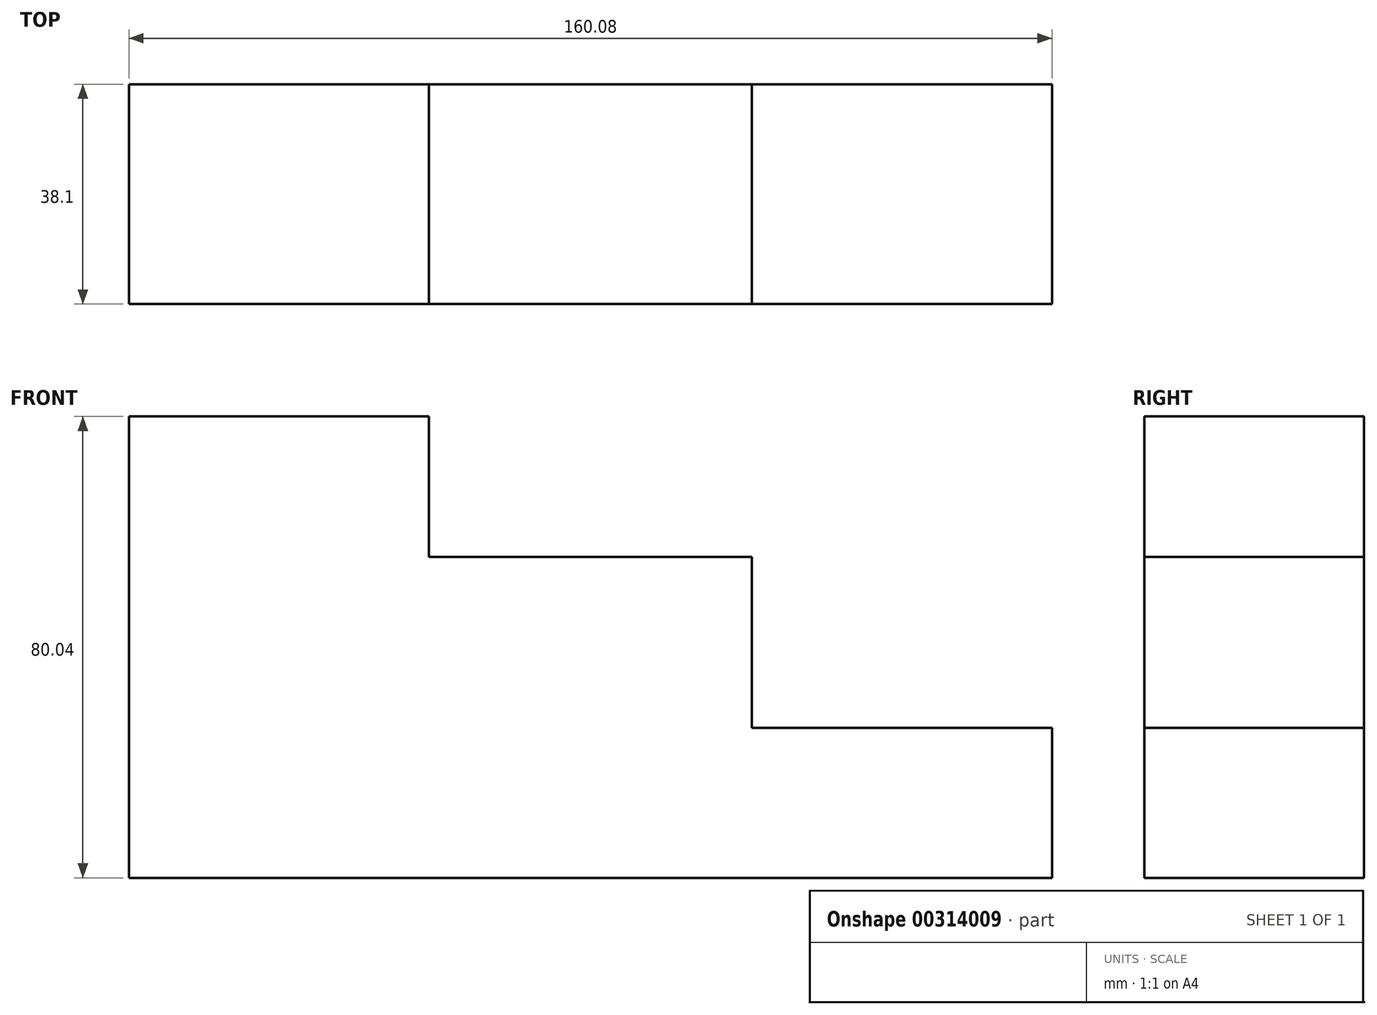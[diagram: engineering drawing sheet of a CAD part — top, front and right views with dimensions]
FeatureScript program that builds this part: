
annotation { "Feature Type Name" : "Feature", "Feature Type Description" : "" }
export const myFeature = defineFeature(function(context is Context, id is Id, definition is map)
    precondition{}
    {
        {
            var Q0;
            Q0=qCreatedBy(makeId("Front.planeOp"),FACE);
            var sketch = newSketch(context, id + "F0", { "sketchPlane" : qUnion([Q0])});
            skLineSegment(sketch, "E0", {"start": v(-72.68, -26.03) * mm, "end": v(87.4, -26.03) * mm});
            skLineSegment(sketch, "E1", {"start": v(-72.68, -26.03) * mm, "end": v(-72.68, 54.01) * mm});
            skLineSegment(sketch, "E2", {"start": v(87.4, -26.03) * mm, "end": v(87.4, 0) * mm});
            skLineSegment(sketch, "E3", {"start": v(87.4, 0) * mm, "end": v(35.38, 0) * mm});
            skLineSegment(sketch, "E4", {"start": v(-72.68, 54.01) * mm, "end": v(-20.65, 54.01) * mm});
            skLineSegment(sketch, "E5", {"start": v(-20.65, 54.01) * mm, "end": v(-20.65, 29.62) * mm});
            skLineSegment(sketch, "E6", {"start": v(-20.65, 29.62) * mm, "end": v(35.38, 29.62) * mm});
            skLineSegment(sketch, "E7", {"start": v(35.38, 29.62) * mm, "end": v(35.38, 0) * mm});
            skSolve(sketch);
        }
        {
            var Q0;
            Q0 = qSketchRegion(id + "F0", true);
            extrude(context, id + "F1", {"entities" : qUnion([Q0]), "depth" : 38.1 * mm});
        }
    });
